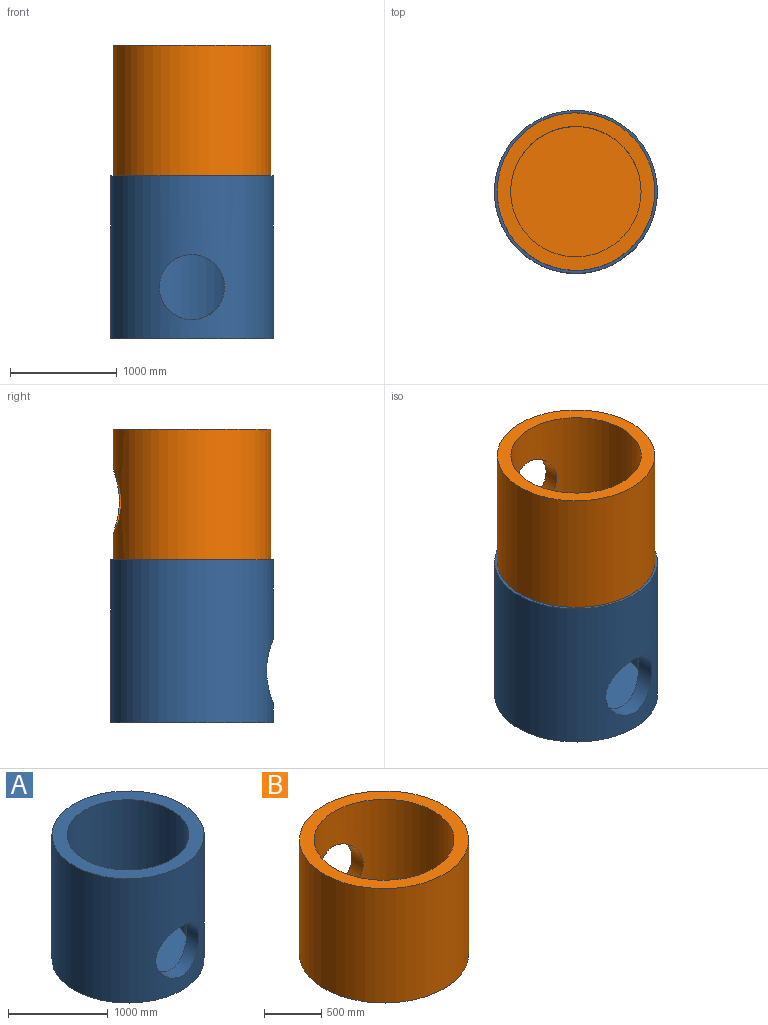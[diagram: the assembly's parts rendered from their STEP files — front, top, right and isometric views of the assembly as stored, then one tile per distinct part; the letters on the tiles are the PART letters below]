
ASSEMBLY  parts=2 mates=1
PART A: 6 faces, bbox 1524x1524x1524 mm
  f0: cylinder r=762mm len=1524mm, axis (0,0,-1), area 6998759.4mm2, adj f2,f3,f5
  f1: cylinder r=609.6mm len=1371.6mm, axis (0,0,1), area 4951510.3mm2, adj f2,f4,f5
  f2: plane 1524x1524mm, normal (0,0,1), area 656692.9mm2, adj f0,f1
  f3: plane 1524x1524mm, normal (0,0,-1), area 1824146.9mm2, adj f0
  f4: plane 1219.2x1219.2mm, normal (0,0,1), area 1167454mm2, adj f1
  f5: cylinder r=304.8mm len=609.6mm, axis (0,1,0), area 308237mm2, adj f0,f1
PART B: 6 faces, bbox 1473.2x1473.2x1219.2 mm
  f0: cylinder r=736.6mm len=1473.2mm, axis (0,0,-1), area 5344742.3mm2, adj f1,f2,f5
  f1: plane 1473.2x1473.2mm, normal (0,0,1), area 537109.9mm2, adj f0,f3
  f2: plane 1473.2x1473.2mm, normal (0,0,-1), area 1704564mm2, adj f0
  f3: cylinder r=609.6mm len=1219.2mm, axis (0,0,1), area 3783825.1mm2, adj f1,f4,f5
  f4: plane 1219.2x1219.2mm, normal (0,0,1), area 1167454mm2, adj f3
  f5: cylinder r=304.8mm len=609.6mm, axis (0,-1,0), area 257939.1mm2, adj f0,f3
PLACE A t=(-665.37,9.29,-171.84)mm
PLACE B t=(-665.37,9.29,1352.16)mm
MATE fastened B.f0 <-> A.f0  axis (0,0,-1) through (-665.37,9.29,1352.16)mm
